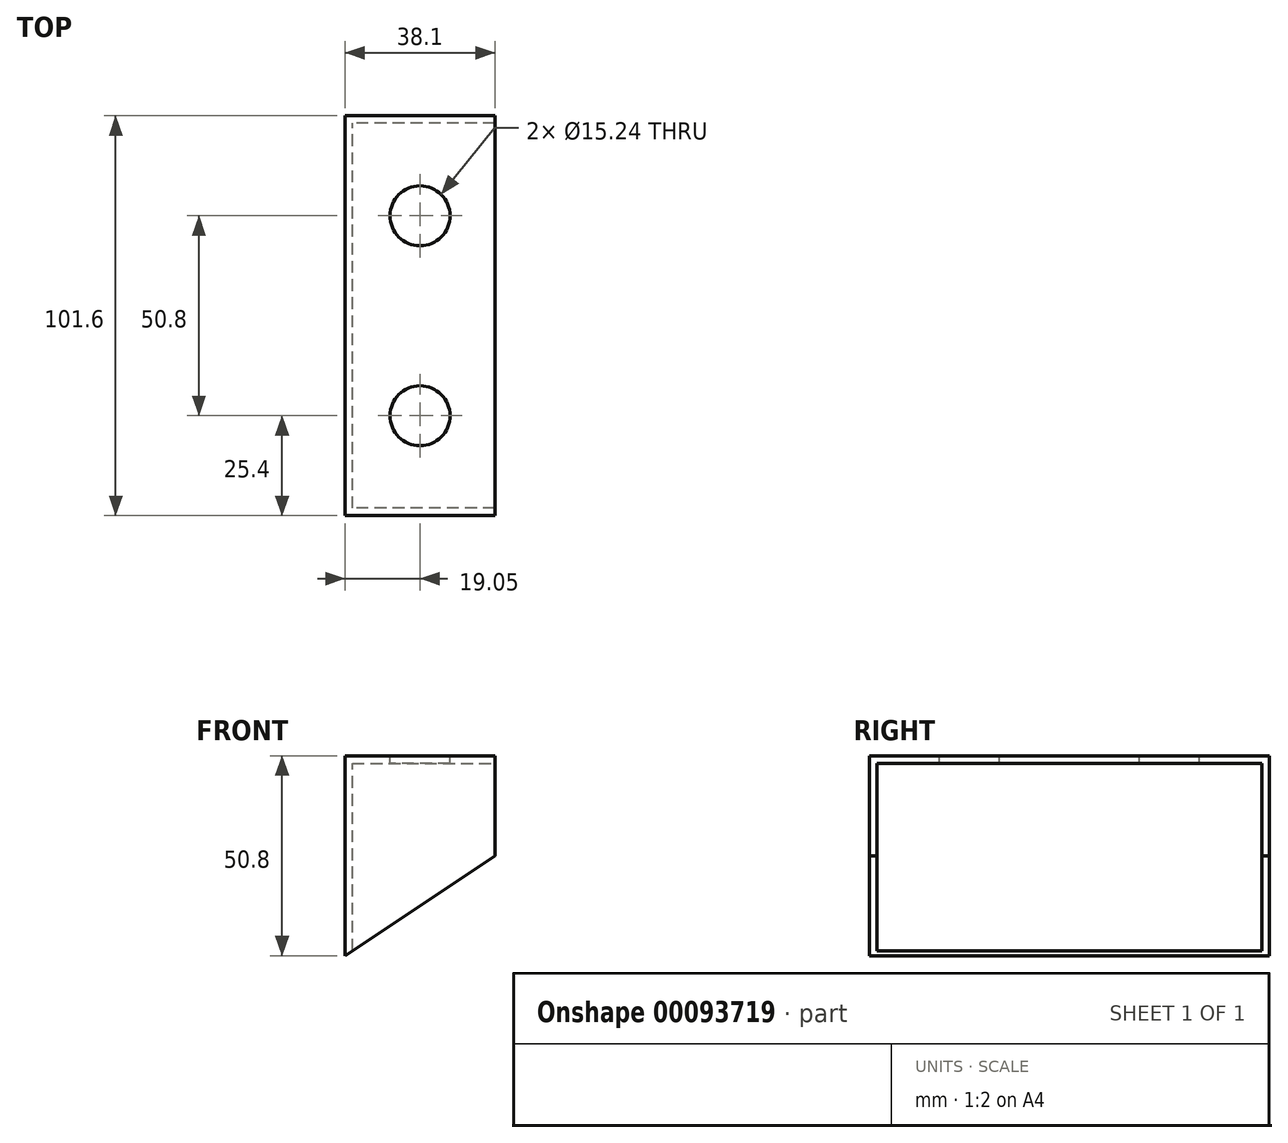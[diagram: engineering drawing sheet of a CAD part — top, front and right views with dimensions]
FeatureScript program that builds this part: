
annotation { "Feature Type Name" : "Feature", "Feature Type Description" : "" }
export const myFeature = defineFeature(function(context is Context, id is Id, definition is map)
    precondition{}
    {
        {
            var Q0;
            Q0=qCreatedBy(makeId("Front.planeOp"),FACE);
            var sketch = newSketch(context, id + "F0", { "sketchPlane" : qUnion([Q0])});
            skLineSegment(sketch, "E0", {"start": v(0, 0) * mm, "end": v(0, 50.8) * mm});
            skLineSegment(sketch, "E1", {"start": v(0, 50.8) * mm, "end": v(38.1, 50.8) * mm});
            skLineSegment(sketch, "E2", {"start": v(38.1, 50.8) * mm, "end": v(38.1, 25.4) * mm});
            skLineSegment(sketch, "E3", {"start": v(38.1, 25.4) * mm, "end": v(0, 0) * mm});
            skSolve(sketch);
        }
        {
            var Q0;
            Q0 = qSketchRegion(id + "F0", true);
            extrude(context, id + "F1", {"entities" : qUnion([Q0]), "endBound" : BoundingType.SYMMETRIC, "depth" : 101.6 * mm});
        }
        {
            var Q0;
            Q0=makeQuery(id+"F1.opExtrude","SWEPT_FACE",FACE,{"disambiguationData":[OSD([sQuery(id+"F0.wireOp",EDGE,"E1")])]});
            var sketch = newSketch(context, id + "F2", { "sketchPlane" : qUnion([Q0])});
            skCircle(sketch, "E4", {"center": v(19.05, 25.4) * mm, "radius": 7.62 * mm});
            skCircle(sketch, "E5", {"center": v(19.05, -25.4) * mm, "radius": 7.62 * mm});
            skLineSegment(sketch, "E6", {"start": v(19.05, 25.4) * mm, "end": v(19.05, -25.4) * mm, "construction": true});
            skSolve(sketch);
        }
        {
            var Q0;
            Q0 = qSketchRegion(id + "F2", true);
            extrude(context, id + "F3", {"entities" : qUnion([Q0]), "operationType" : NewBodyOperationType.REMOVE, "endBound" : BoundingType.THROUGH_ALL, "oppositeDirection" : true, "depth" : 25.4 * mm});
        }
        {
            var Q0;
            Q0=makeQuery(id+"F1.opExtrude","SWEPT_FACE",FACE,{"disambiguationData":[OSD([sQuery(id+"F0.wireOp",EDGE,"E3")])]});
            var Q1;
            Q1=makeQuery(id+"F1.opExtrude","SWEPT_FACE",FACE,{"disambiguationData":[OSD([sQuery(id+"F0.wireOp",EDGE,"E2")])]});
            var Q2;
            Q2=makeQuery(id+"F3.boolean.opBoolean","COPY",FACE,{"derivedFrom":makeQuery(id+"F3.opExtrude","SWEPT_FACE",FACE,{"disambiguationData":[OSD([sQuery(id+"F2.wireOp",EDGE,"E5")])]})});
            var Q3;
            Q3=makeQuery(id+"F3.boolean.opBoolean","COPY",FACE,{"derivedFrom":makeQuery(id+"F3.opExtrude","SWEPT_FACE",FACE,{"disambiguationData":[OSD([sQuery(id+"F2.wireOp",EDGE,"E4")])]})});
            shell(context, id + "F4", {"entities" : qUnion([Q0, Q1, Q2, Q3]), "thickness" : 1.9 * mm});
        }
    });
